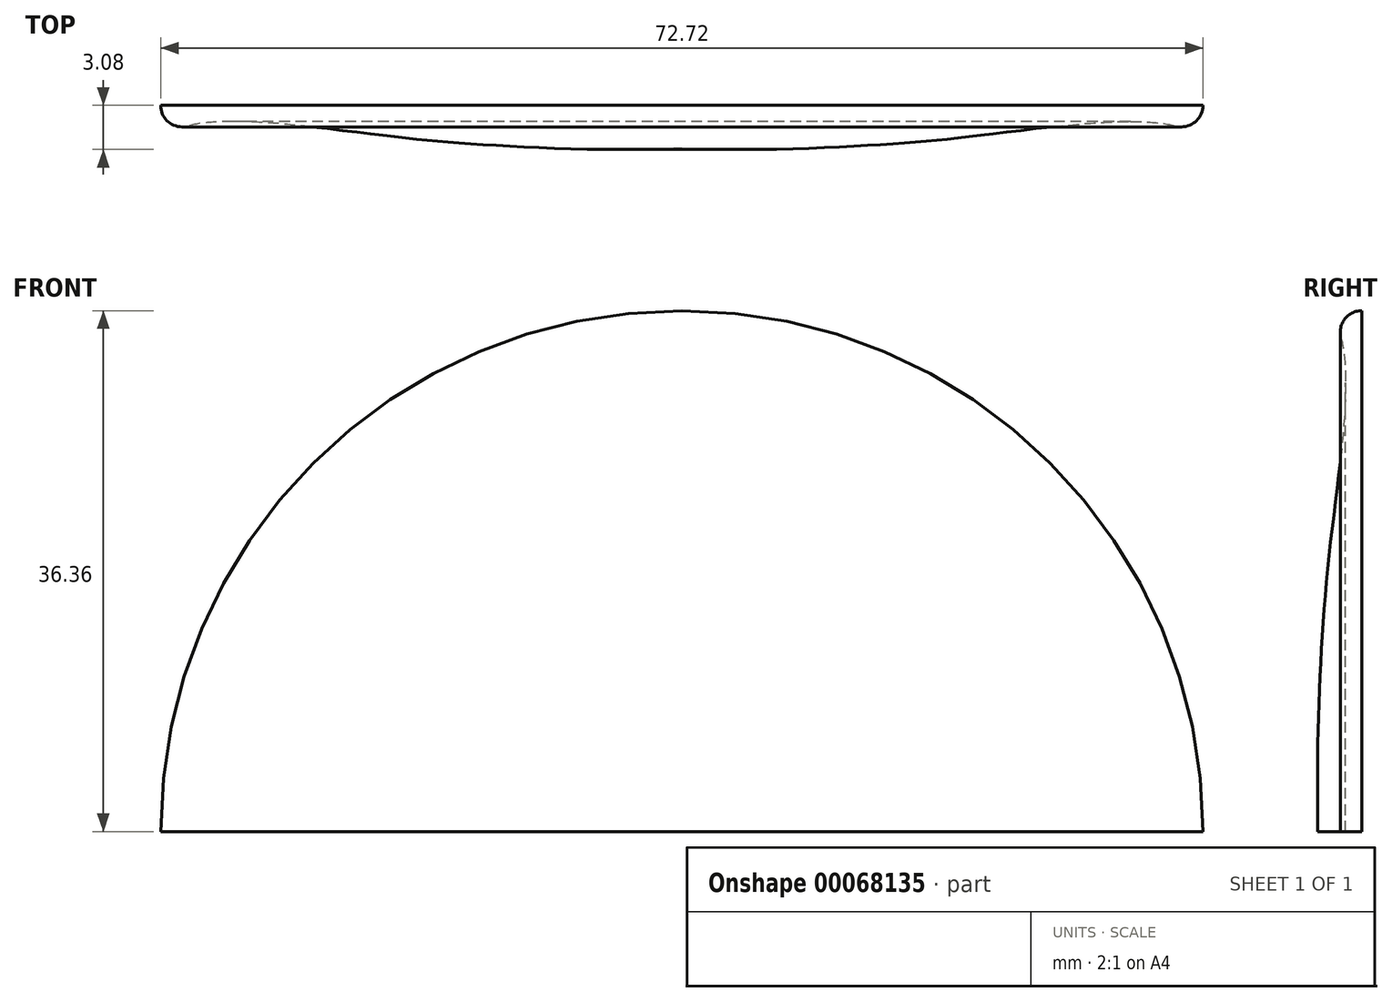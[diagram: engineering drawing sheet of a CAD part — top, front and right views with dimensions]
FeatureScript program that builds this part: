
annotation { "Feature Type Name" : "Feature", "Feature Type Description" : "" }
export const myFeature = defineFeature(function(context is Context, id is Id, definition is map)
    precondition{}
    {
        {
            var Q0;
            Q0=qCreatedBy(makeId("Top.planeOp"),FACE);
            var sketch = newSketch(context, id + "F0", { "sketchPlane" : qUnion([Q0])});
            skLineSegment(sketch, "E0", {"start": v(0, 0) * mm, "end": v(0, 3) * mm});
            skArc(sketch, "E1", {"start": v(36.36, 0) * mm, "mid": v(35.76, 1.2) * mm, "end": v(34.45, 1.44) * mm});
            skFitSpline(sketch, "E2", {"points": [v(0, 3) * mm, v(14.64, 2.68) * mm, v(22.18, 1.94) * mm, v(34.45, 1.44) * mm], "startDerivative": vector(44, 1.75) * mm, "endDerivative": vector(23.44, 6.54) * mm});
            skLineSegment(sketch, "E3", {"start": v(0, 0) * mm, "end": v(36.36, 0) * mm, "construction": true});
            skLineSegment(sketch, "E4.MirrorCS", {"start": v(0, 0) * mm, "end": v(0, -3) * mm});
            skFitSpline(sketch, "E5.MirrorCS", {"points": [v(0, -3) * mm, v(14.64, -2.68) * mm, v(22.18, -1.94) * mm, v(34.45, -1.44) * mm], "startDerivative": vector(44, -1.75) * mm, "endDerivative": vector(23.44, -6.54) * mm});
            skArc(sketch, "E6.MirrorCS", {"start": v(36.36, 0) * mm, "mid": v(35.76, -1.2) * mm, "end": v(34.45, -1.44) * mm});
            skSolve(sketch);
        }
        {
            var Q0;
            Q0 = qSketchRegion(id + "F0", true);
            var Q1;
            Q1=sQuery(id+"F0.wireOp",EDGE,"E4.MirrorCS");
            revolve(context, id + "F1", {"entities" : qUnion([Q0]), "axis" : qUnion([Q1]), "revolveType" : RevolveType.ONE_DIRECTION, "angle" : 180 * degree});
        }
        {
            var Q0;
            Q0=makeQuery(id+"F1.opRevolve","CAP_FACE",FACE,{"disambiguationData":[OSD([sQuery(id+"F0.wireOp",EDGE,"E0"),sQuery(id+"F0.wireOp",EDGE,"E1"),sQuery(id+"F0.wireOp",EDGE,"E2"),sQuery(id+"F0.wireOp",EDGE,"E4.MirrorCS"),sQuery(id+"F0.wireOp",EDGE,"E5.MirrorCS"),sQuery(id+"F0.wireOp",EDGE,"E6.MirrorCS")])],"isStart":true});
            var sketch = newSketch(context, id + "F2", { "sketchPlane" : qUnion([Q0])});
            skPoint(sketch, "E7.firstSnap0", {"position": v(-36.36, 0) * mm});
            skLineSegment(sketch, "E7.bottom", {"start": v(-39.63, 0) * mm, "end": v(52.67, 0) * mm});
            skLineSegment(sketch, "E7.top", {"start": v(-39.63, -7.19) * mm, "end": v(52.67, -7.19) * mm});
            skLineSegment(sketch, "E7.left", {"start": v(-39.63, 0) * mm, "end": v(-39.63, -7.19) * mm});
            skLineSegment(sketch, "E7.right", {"start": v(52.67, 0) * mm, "end": v(52.67, -7.19) * mm});
            skSolve(sketch);
        }
        {
            var Q0;
            Q0 = qSketchRegion(id + "F2", true);
            extrude(context, id + "F3", {"entities" : qUnion([Q0]), "operationType" : NewBodyOperationType.REMOVE, "endBound" : BoundingType.THROUGH_ALL, "oppositeDirection" : true, "depth" : 25 * mm});
        }
    });
